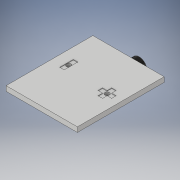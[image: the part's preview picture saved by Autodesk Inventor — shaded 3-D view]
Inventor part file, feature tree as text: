
AUTODESK INVENTOR PART (.ipt)
format: ipt  version: 2018 (Build 220112000, 112)  size: 200,704 bytes
history: native  units: in
note: dims shown in document units (in); Inventor stores cm internally (conversion verified against a paired STEP export)
features: extrude x5, sketch x4, mirror x1, direct_edit x1, other x1, move_body x1
ambient origin geometry x8: Origin, YZ Plane, XZ Plane, XY Plane, X Axis, Y Axis, Z Axis, Center Point
bodies: Solid1 (feature_tree), Solid2 (feature_tree)
feature tree (13):
  extrude  "Extrusion1"  Depth=0.92in
  extrude  "Extrusion2"  Depth=0.2362in
  extrude  "Extrusion3"  Depth=0.3543in
  mirror  "Mirror1"
  sketch  "Sketch4"  dims[d7=0.0315in d8=0.1969in d9=0.0in d10=0.1969in d11=0.1181in d12=0.0984in d13=0.1378in d14=0.0945in d15=0.0in d16=0.0591in d17=0.1693in d18=0.4803in d19=0.185in d20=0.5512in d21=0.0591in d22=0.1772in d23=0.1772in d24=0.0591in d25=0.0591in d26=0.1772in d27=0.0945in d28=0.0in d29=0.0079in d30=0.0in d31=0.0in d32=0.0in d33=-0.0079in]
  extrude  "Extrusion4"  Depth=0.1969in TaperAngle=0.0deg
  extrude  "Extrusion5"  Depth=0.1969in
  direct_edit  "Direct Edit1"
  sketch  "Sketch1"  dims[d0=1.12in d1=0.92in]
  sketch  "Sketch2"  dims[d2=0.063in d3=0.0in d4=0.2362in]
  sketch  "Sketch3"  dims[d5=0.5906in d6=0.3543in]
  other  "Pattern of Solid1:1"
  move_body  "Move1"
